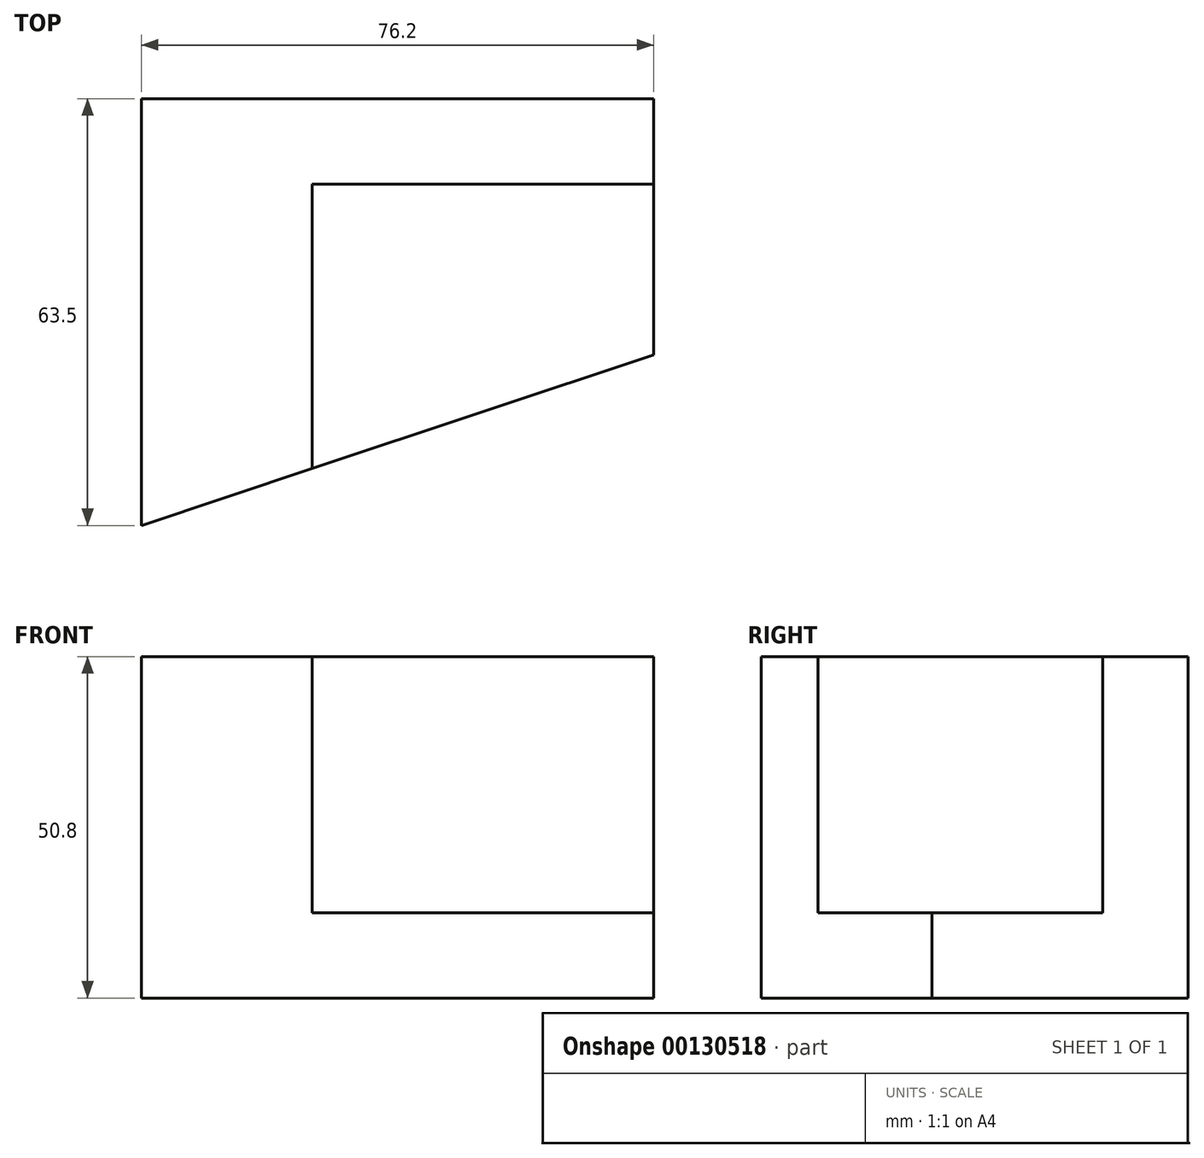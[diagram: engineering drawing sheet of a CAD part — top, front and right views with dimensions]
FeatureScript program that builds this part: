
annotation { "Feature Type Name" : "Feature", "Feature Type Description" : "" }
export const myFeature = defineFeature(function(context is Context, id is Id, definition is map)
    precondition{}
    {
        {
            var Q0;
            Q0=qCreatedBy(makeId("Top.planeOp"),FACE);
            var sketch = newSketch(context, id + "F0", { "sketchPlane" : qUnion([Q0])});
            skLineSegment(sketch, "E0", {"start": v(0, 63.5) * mm, "end": v(0, 0) * mm});
            skLineSegment(sketch, "E1", {"start": v(0, 0) * mm, "end": v(76.2, 25.4) * mm});
            skLineSegment(sketch, "E2", {"start": v(76.2, 25.4) * mm, "end": v(76.2, 63.5) * mm});
            skLineSegment(sketch, "E3", {"start": v(76.2, 63.5) * mm, "end": v(0, 63.5) * mm});
            skSolve(sketch);
        }
        {
            var Q0;
            Q0 = qSketchRegion(id + "F0", true);
            extrude(context, id + "F1", {"entities" : qUnion([Q0]), "depth" : 50.8 * mm});
        }
        {
            var Q0;
            Q0=makeQuery(id+"F1.opExtrude","CAP_FACE",FACE,{"disambiguationData":[OSD([sQuery(id+"F0.wireOp",EDGE,"E0"),sQuery(id+"F0.wireOp",EDGE,"E1"),sQuery(id+"F0.wireOp",EDGE,"E2"),sQuery(id+"F0.wireOp",EDGE,"E3")])],"isStart":false});
            var sketch = newSketch(context, id + "F2", { "sketchPlane" : qUnion([Q0])});
            skLineSegment(sketch, "E4", {"start": v(76.2, 50.8) * mm, "end": v(25.4, 50.8) * mm});
            skLineSegment(sketch, "E5", {"start": v(25.4, 50.8) * mm, "end": v(25.4, 8.47) * mm});
            skLineSegment(sketch, "E6", {"start": v(25.4, 8.47) * mm, "end": v(76.2, 25.4) * mm});
            skLineSegment(sketch, "E7", {"start": v(76.2, 25.4) * mm, "end": v(76.2, 50.8) * mm});
            skSolve(sketch);
        }
        {
            var Q0;
            Q0 = qSketchRegion(id + "F2", true);
            extrude(context, id + "F3", {"entities" : qUnion([Q0]), "operationType" : NewBodyOperationType.REMOVE, "oppositeDirection" : true, "depth" : 38.1 * mm});
        }
    });
